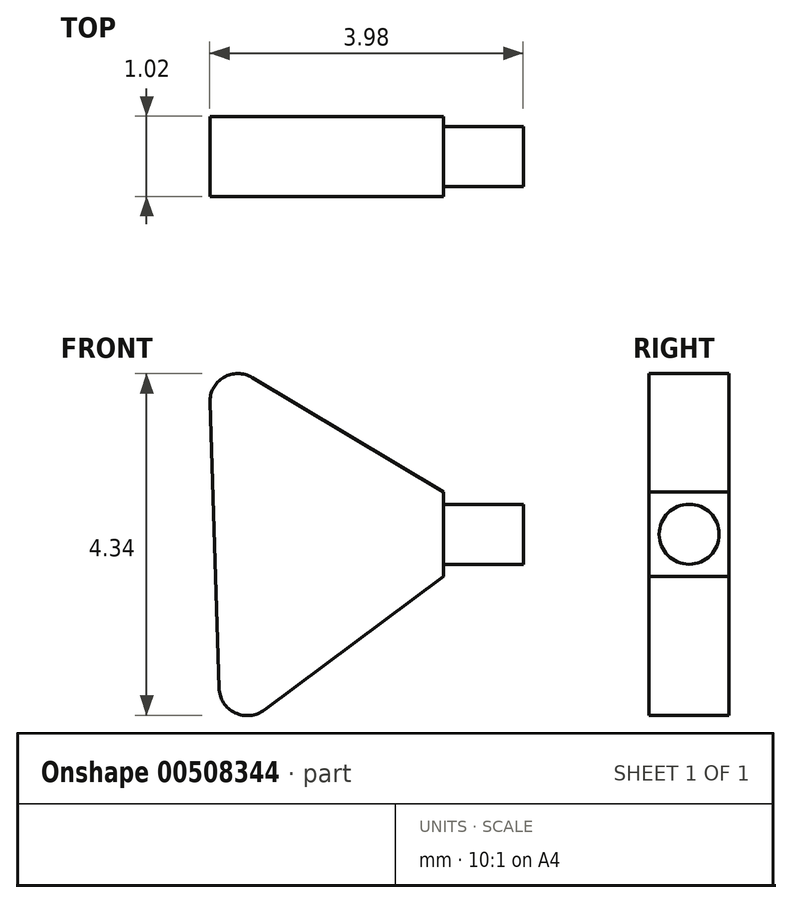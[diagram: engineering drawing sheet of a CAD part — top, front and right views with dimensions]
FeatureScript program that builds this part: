
annotation { "Feature Type Name" : "Feature", "Feature Type Description" : "" }
export const myFeature = defineFeature(function(context is Context, id is Id, definition is map)
    precondition{}
    {
        {
            var Q0;
            Q0=qCreatedBy(makeId("Front.planeOp"),FACE);
            var sketch = newSketch(context, id + "F0", { "sketchPlane" : qUnion([Q0])});
            skLineSegment(sketch, "E0", {"start": v(-9.24, 63.74) * mm, "end": v(-9.08, 58.77) * mm});
            skLineSegment(sketch, "E1", {"start": v(-9.08, 58.77) * mm, "end": v(-6.25, 60.88) * mm});
            skLineSegment(sketch, "E2", {"start": v(-6.25, 60.88) * mm, "end": v(-6.25, 61.96) * mm});
            skLineSegment(sketch, "E3", {"start": v(-6.25, 61.96) * mm, "end": v(-9.24, 63.74) * mm});
            skSolve(sketch);
        }
        {
            var Q0;
            Q0 = qSketchRegion(id + "F0", true);
            extrude(context, id + "F1", {"entities" : qUnion([Q0]), "depth" : 1.02 * mm, "symmetric" : true});
        }
        {
            var Q0;
            Q0=makeQuery(id+"F1.opExtrude","SWEPT_FACE",FACE,{"disambiguationData":[OSD([sQuery(id+"F0.wireOp",EDGE,"E2")])]});
            var sketch = newSketch(context, id + "F2", { "sketchPlane" : qUnion([Q0])});
            skCircle(sketch, "E4", {"center": v(0, 61.42) * mm, "radius": 0.38 * mm});
            skSolve(sketch);
        }
        {
            var Q0;
            Q0 = qSketchRegion(id + "F2", true);
            extrude(context, id + "F3", {"entities" : qUnion([Q0]), "operationType" : NewBodyOperationType.ADD, "depth" : 1.02 * mm, "offsetDistance" : 25.4 * mm});
        }
        {
            var Q0;
            Q0=makeQuery(id+"F1.opExtrude","SWEPT_EDGE",EDGE,{"disambiguationData":[OSD([sQuery(id+"F0.wireOp",EDGE,"E0"),sQuery(id+"F0.wireOp",EDGE,"E1")])]});
            fillet(context, id + "F4", {"entities" : qUnion([Q0]), "radius" : 0.36 * mm, "tangentPropagation" : true, "allowEdgeOverflow" : false});
        }
        {
            var Q0;
            Q0=makeQuery(id+"F1.opExtrude","SWEPT_EDGE",EDGE,{"disambiguationData":[OSD([sQuery(id+"F0.wireOp",EDGE,"E0"),sQuery(id+"F0.wireOp",EDGE,"E3")])]});
            fillet(context, id + "F5", {"entities" : qUnion([Q0]), "radius" : 0.36 * mm, "tangentPropagation" : true, "allowEdgeOverflow" : false});
        }
    });
